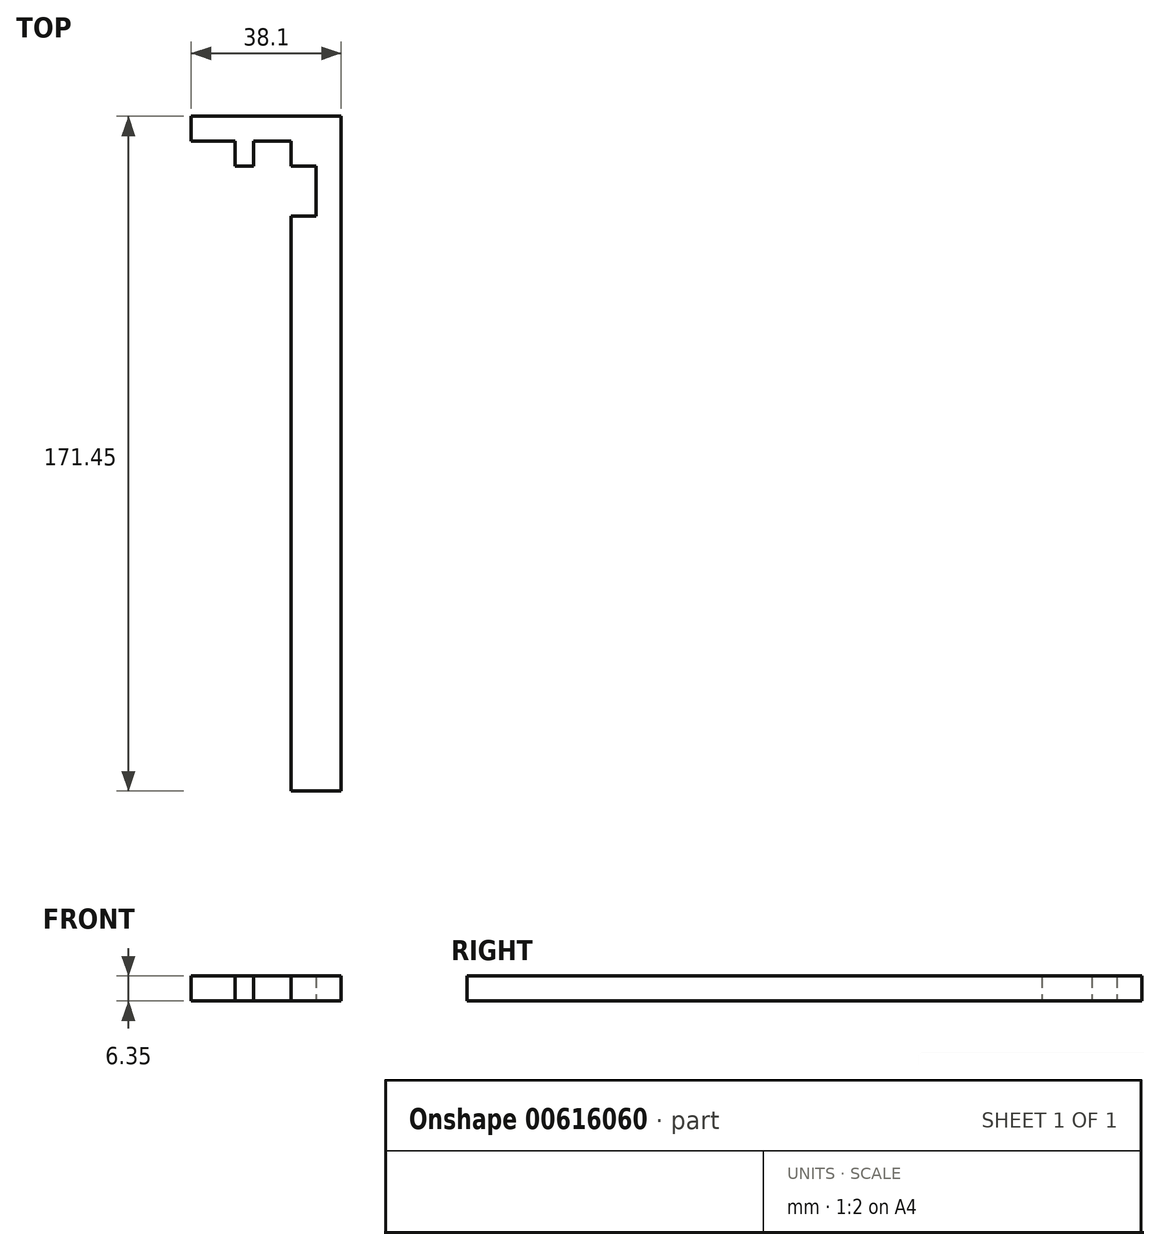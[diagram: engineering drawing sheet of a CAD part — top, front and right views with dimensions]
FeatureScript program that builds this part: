
annotation { "Feature Type Name" : "Feature", "Feature Type Description" : "" }
export const myFeature = defineFeature(function(context is Context, id is Id, definition is map)
    precondition{}
    {
        {
            var Q0;
            Q0=qCreatedBy(makeId("Top.planeOp"),FACE);
            var sketch = newSketch(context, id + "F0", { "sketchPlane" : qUnion([Q0])});
            skLineSegment(sketch, "E0.bottom", {"start": v(7.84, 15.69) * mm, "end": v(1.5, 15.69) * mm});
            skLineSegment(sketch, "E0.top", {"start": v(7.84, -136.71) * mm, "end": v(1.5, -136.71) * mm});
            skLineSegment(sketch, "E0.left", {"start": v(7.84, 15.69) * mm, "end": v(7.84, -136.71) * mm});
            skPoint(sketch, "E0.middle", {"position": v(1.5, -60.51) * mm});
            skLineSegment(sketch, "E1.top", {"start": v(7.84, 22.04) * mm, "end": v(1.5, 22.04) * mm});
            skLineSegment(sketch, "E1.left", {"start": v(7.84, 15.69) * mm, "end": v(7.84, 22.04) * mm});
            skLineSegment(sketch, "E1.right", {"start": v(1.5, 15.69) * mm, "end": v(1.5, 22.04) * mm});
            skLineSegment(sketch, "E2.bottom", {"start": v(7.84, 22.04) * mm, "end": v(-4.86, 22.04) * mm});
            skLineSegment(sketch, "E2.top", {"start": v(7.84, 28.39) * mm, "end": v(-4.86, 28.39) * mm});
            skLineSegment(sketch, "E2.left", {"start": v(7.84, 22.04) * mm, "end": v(7.84, 28.39) * mm});
            skLineSegment(sketch, "E2.right", {"start": v(-4.86, 22.04) * mm, "end": v(-4.86, 28.39) * mm});
            skLineSegment(sketch, "E3.bottom", {"start": v(7.84, 28.39) * mm, "end": v(-30.26, 28.39) * mm});
            skLineSegment(sketch, "E3.top", {"start": v(7.84, 34.74) * mm, "end": v(-30.26, 34.74) * mm});
            skLineSegment(sketch, "E3.left", {"start": v(7.84, 28.39) * mm, "end": v(7.84, 34.74) * mm});
            skLineSegment(sketch, "E3.right", {"start": v(-30.26, 28.39) * mm, "end": v(-30.26, 34.74) * mm});
            skLineSegment(sketch, "E4.bottom", {"start": v(-14.38, 28.39) * mm, "end": v(-19.14, 28.39) * mm});
            skLineSegment(sketch, "E4.top", {"start": v(-14.38, 22.04) * mm, "end": v(-19.14, 22.04) * mm});
            skLineSegment(sketch, "E4.left", {"start": v(-14.38, 28.39) * mm, "end": v(-14.38, 22.04) * mm});
            skLineSegment(sketch, "E4.right", {"start": v(-19.14, 28.39) * mm, "end": v(-19.14, 22.04) * mm});
            skLineSegment(sketch, "E5.left", {"start": v(1.5, 15.69) * mm, "end": v(1.5, -136.71) * mm});
            skLineSegment(sketch, "E6.bottom", {"start": v(1.5, -136.71) * mm, "end": v(-4.86, -136.71) * mm});
            skLineSegment(sketch, "E6.top", {"start": v(1.5, 9.34) * mm, "end": v(-4.86, 9.34) * mm});
            skLineSegment(sketch, "E6.left", {"start": v(1.5, -136.71) * mm, "end": v(1.5, 9.34) * mm});
            skLineSegment(sketch, "E6.right", {"start": v(-4.86, -136.71) * mm, "end": v(-4.86, 9.34) * mm});
            skSolve(sketch);
        }
        {
            var Q0;
            Q0 = qSketchRegion(id + "F0", true);
            extrude(context, id + "F1", {"entities" : qUnion([Q0]), "depth" : 6.35 * mm, "offsetDistance" : 25.4 * mm});
        }
    });
